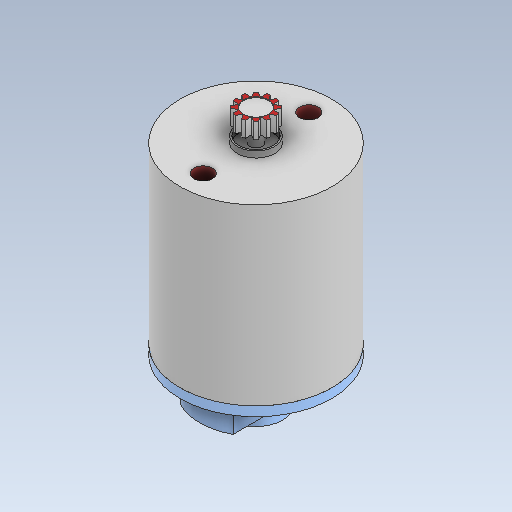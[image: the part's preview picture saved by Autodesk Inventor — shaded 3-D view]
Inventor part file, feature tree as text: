
AUTODESK INVENTOR PART (.ipt)
format: ipt  version: 2020 (Build 240168000, 168)  size: 236,032 bytes
history: native  units: mm
features: extrude x11, sketch x11, other x2, pattern_circular x1
ambient origin geometry x8: Origin, YZ Plane, XZ Plane, XY Plane, X Axis, Y Axis, Z Axis, Center Point
bodies: Body1 (feature_tree), Body2 (feature_tree)
feature tree (25):
  other  "Bryła1"
  extrude  "Wyciągnięcie proste1"  Depth=24.4mm
  extrude  "Wyciągnięcie proste2"  Depth=28.0mm TaperAngle=0.0deg
  extrude  "Wyciągnięcie proste3"  Depth=6.0mm
  extrude  "Wyciągnięcie proste4"  Depth=1.0mm TaperAngle=0.0deg
  extrude  "Wyciągnięcie proste5"  Depth=5.5mm
  extrude  "Wyciągnięcie proste6"  Depth=1.0mm TaperAngle=0.0deg
  extrude  "Wyciągnięcie proste7"  Depth=2.0mm
  pattern_circular  "Szyk kołowy1"  [2 undecoded]
  extrude  "Wyciągnięcie proste8"  Depth=5.75mm
  extrude  "Wyciągnięcie proste9"  Depth=2.5mm TaperAngle=0.0deg
  extrude  "Wyciągnięcie proste10"  Depth=4.0mm
  extrude  "Wyciągnięcie proste11"  TaperAngle=30.0deg  [1 undecoded]
  sketch  "Szkic1"
  sketch  "Szkic2"
  sketch  "Szkic3"
  sketch  "Szkic4"
  sketch  "Szkic5"
  sketch  "Szkic6"
  sketch  "Szkic7"
  sketch  "Szkic8"
  sketch  "Szkic9"
  other  "Bryła2"
  sketch  "Szkic10"
  sketch  "Szkic11"
note: 3 required parameter values undecoded (feature->parameter linkage not recoverable at this tier; creation-order binding heuristic only, values carry confidence <= 0.55)
